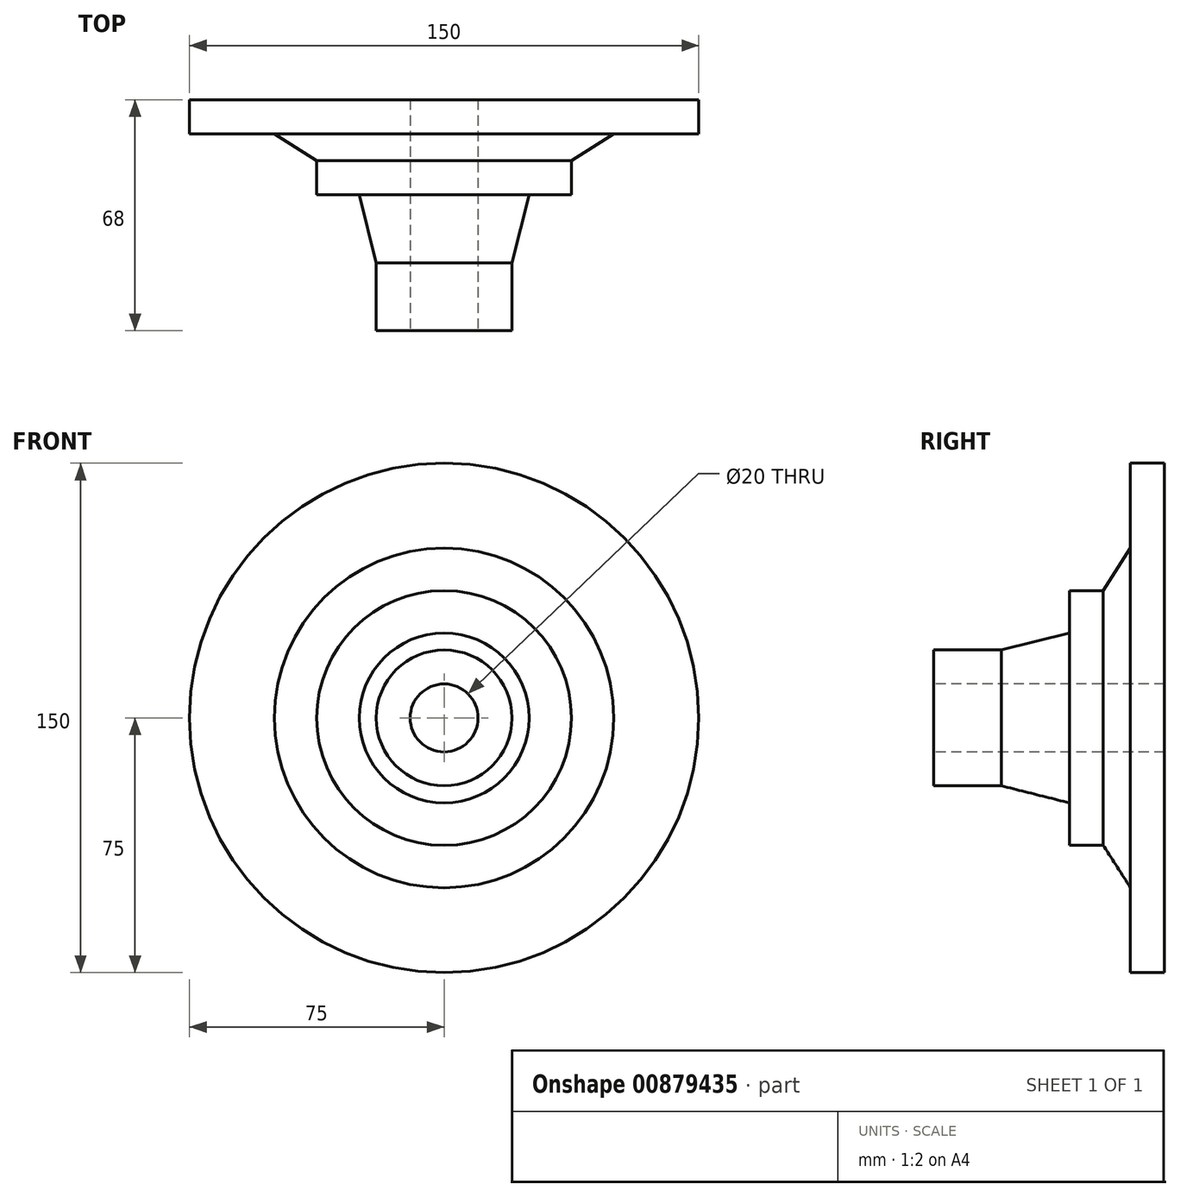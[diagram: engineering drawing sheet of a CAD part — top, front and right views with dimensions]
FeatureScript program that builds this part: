
annotation { "Feature Type Name" : "Feature", "Feature Type Description" : "" }
export const myFeature = defineFeature(function(context is Context, id is Id, definition is map)
    precondition{}
    {
        {
            var Q0;
            Q0=qCreatedBy(makeId("Right.planeOp"),FACE);
            var sketch = newSketch(context, id + "F0", { "sketchPlane" : qUnion([Q0])});
            skLineSegment(sketch, "E0", {"start": v(-46.42, -25) * mm, "end": v(21.58, -25) * mm});
            skLineSegment(sketch, "E1", {"start": v(-46.42, -15) * mm, "end": v(21.58, -15) * mm});
            skLineSegment(sketch, "E2", {"start": v(21.58, -15) * mm, "end": v(21.58, 50) * mm});
            skLineSegment(sketch, "E3", {"start": v(-46.42, -15) * mm, "end": v(-46.42, -5) * mm});
            skLineSegment(sketch, "E4", {"start": v(-46.42, -5) * mm, "end": v(-26.42, -5) * mm});
            skLineSegment(sketch, "E5", {"start": v(-26.42, -5) * mm, "end": v(-6.42, 0) * mm});
            skLineSegment(sketch, "E6", {"start": v(-6.42, 0) * mm, "end": v(-6.42, 12.5) * mm});
            skLineSegment(sketch, "E7", {"start": v(-6.42, 12.5) * mm, "end": v(3.58, 12.5) * mm});
            skLineSegment(sketch, "E8", {"start": v(3.58, 12.5) * mm, "end": v(11.58, 25) * mm});
            skLineSegment(sketch, "E9", {"start": v(11.58, 25) * mm, "end": v(11.58, 50) * mm});
            skLineSegment(sketch, "E10", {"start": v(11.58, 50) * mm, "end": v(21.58, 50) * mm});
            skSolve(sketch);
        }
        {
            var Q0;
            Q0=makeQuery(id+"F0.imprint","IMPRINT",FACE,{"disambiguationData":[TD([[makeQuery(id+"F0.imprint","IMPRINT",EDGE,{"derivedFrom":sQuery(id+"F0.wireOp",EDGE,"E1")}),1.0]])]});
            var Q1;
            Q1=sQuery(id+"F0.wireOp",EDGE,"E0");
            revolve(context, id + "F1", {"surfaceOperationType" : NewSurfaceOperationType.NEW, "entities" : qUnion([Q0]), "axis" : qUnion([Q1]), "revolveType" : RevolveType.FULL});
        }
    });
